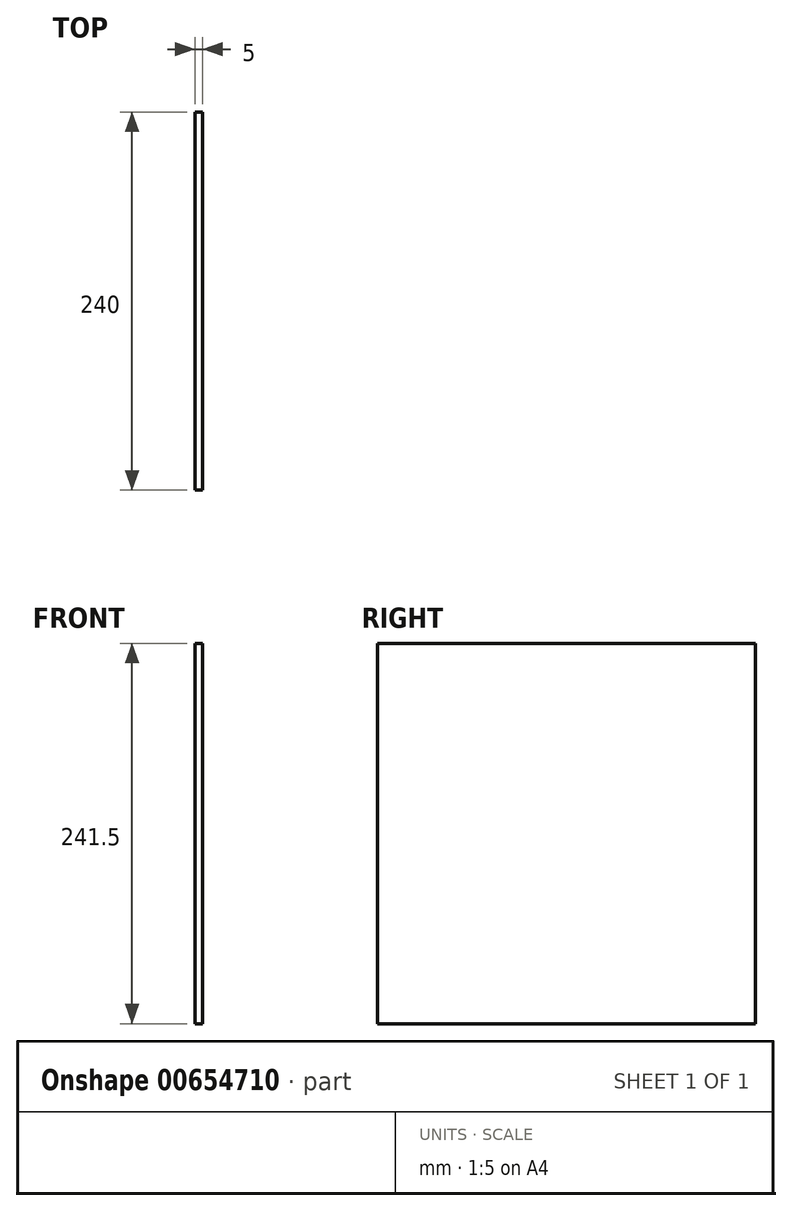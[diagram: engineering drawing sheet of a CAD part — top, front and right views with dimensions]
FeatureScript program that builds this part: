
annotation { "Feature Type Name" : "Feature", "Feature Type Description" : "" }
export const myFeature = defineFeature(function(context is Context, id is Id, definition is map)
    precondition{}
    {
        {
            var Q0;
            Q0=qCreatedBy(makeId("Top.planeOp"),FACE);
            var sketch = newSketch(context, id + "F0", { "sketchPlane" : qUnion([Q0])});
            skLineSegment(sketch, "E0.bottom", {"start": v(100, 190) * mm, "end": v(95, 190) * mm});
            skLineSegment(sketch, "E0.top", {"start": v(100, -50) * mm, "end": v(95, -50) * mm});
            skLineSegment(sketch, "E0.left", {"start": v(100, 190) * mm, "end": v(100, -50) * mm});
            skLineSegment(sketch, "E0.right", {"start": v(95, 190) * mm, "end": v(95, -50) * mm});
            skSolve(sketch);
        }
        {
            var Q0;
            Q0 = qSketchRegion(id + "F0", true);
            extrude(context, id + "F1", {"entities" : qUnion([Q0]), "depth" : 241.5 * mm, "offsetDistance" : 25 * mm});
        }
    });
